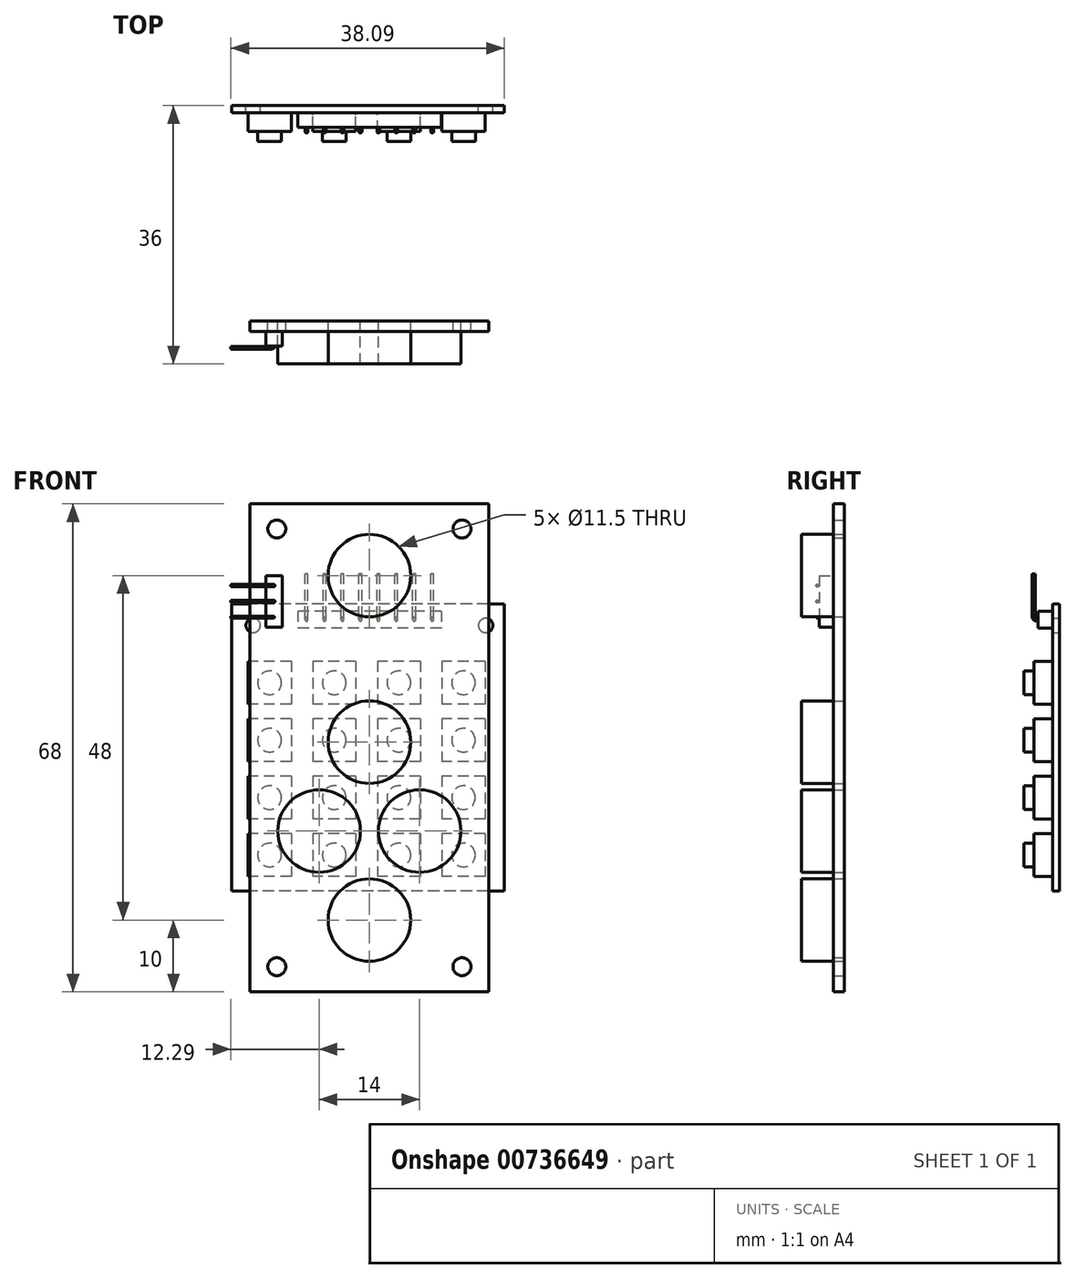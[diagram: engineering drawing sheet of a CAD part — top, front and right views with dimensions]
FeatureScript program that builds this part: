
annotation { "Feature Type Name" : "Feature", "Feature Type Description" : "" }
export const myFeature = defineFeature(function(context is Context, id is Id, definition is map)
    precondition{}
    {
        {
            var Q0;
            Q0=qCreatedBy(makeId("Front.planeOp"),FACE);
            var sketch = newSketch(context, id + "F0", { "sketchPlane" : qUnion([Q0])});
            skLineSegment(sketch, "E0.bottom", {"start": v(18.8, 20.06) * mm, "end": v(-19.2, 20.06) * mm});
            skLineSegment(sketch, "E0.top", {"start": v(18.8, -19.94) * mm, "end": v(-19.2, -19.94) * mm});
            skLineSegment(sketch, "E0.left", {"start": v(18.8, 20.06) * mm, "end": v(18.8, -19.94) * mm});
            skLineSegment(sketch, "E0.right", {"start": v(-19.2, 20.06) * mm, "end": v(-19.2, -19.94) * mm});
            skCircle(sketch, "E1", {"center": v(-16.2, 17.06) * mm, "radius": 1 * mm});
            skCircle(sketch, "E2.MirrorC", {"center": v(16.2, 17.06) * mm, "radius": 1 * mm});
            skLineSegment(sketch, "E3.bottom", {"start": v(-10.9, 12.06) * mm, "end": v(-16.9, 12.06) * mm});
            skLineSegment(sketch, "E3.top", {"start": v(-10.9, 6.06) * mm, "end": v(-16.9, 6.06) * mm});
            skLineSegment(sketch, "E3.left", {"start": v(-10.9, 12.06) * mm, "end": v(-10.9, 6.06) * mm});
            skLineSegment(sketch, "E3.right", {"start": v(-16.9, 12.06) * mm, "end": v(-16.9, 6.06) * mm});
            skPoint(sketch, "E3.middle", {"position": v(-13.9, 9.06) * mm});
            skCircle(sketch, "E4", {"center": v(-13.9, 9.06) * mm, "radius": 1.65 * mm});
            skLineSegment(sketch, "E5.0.1.0", {"start": v(-10.9, 4.06) * mm, "end": v(-10.9, -1.94) * mm});
            skLineSegment(sketch, "E5.0.1.1", {"start": v(-10.9, -1.94) * mm, "end": v(-16.9, -1.94) * mm});
            skLineSegment(sketch, "E5.0.1.2", {"start": v(-16.9, 4.06) * mm, "end": v(-16.9, -1.94) * mm});
            skLineSegment(sketch, "E5.0.1.3", {"start": v(-10.9, 4.06) * mm, "end": v(-16.9, 4.06) * mm});
            skCircle(sketch, "E5.0.1.4", {"center": v(-13.9, 1.06) * mm, "radius": 1.65 * mm});
            skLineSegment(sketch, "E5.0.2.0", {"start": v(-10.9, -3.94) * mm, "end": v(-10.9, -9.94) * mm});
            skLineSegment(sketch, "E5.0.2.1", {"start": v(-10.9, -9.94) * mm, "end": v(-16.9, -9.94) * mm});
            skLineSegment(sketch, "E5.0.2.2", {"start": v(-16.9, -3.94) * mm, "end": v(-16.9, -9.94) * mm});
            skLineSegment(sketch, "E5.0.2.3", {"start": v(-10.9, -3.94) * mm, "end": v(-16.9, -3.94) * mm});
            skCircle(sketch, "E5.0.2.4", {"center": v(-13.9, -6.94) * mm, "radius": 1.65 * mm});
            skLineSegment(sketch, "E5.0.3.0", {"start": v(-10.9, -11.94) * mm, "end": v(-10.9, -17.94) * mm});
            skLineSegment(sketch, "E5.0.3.1", {"start": v(-10.9, -17.94) * mm, "end": v(-16.9, -17.94) * mm});
            skLineSegment(sketch, "E5.0.3.2", {"start": v(-16.9, -11.94) * mm, "end": v(-16.9, -17.94) * mm});
            skLineSegment(sketch, "E5.0.3.3", {"start": v(-10.9, -11.94) * mm, "end": v(-16.9, -11.94) * mm});
            skCircle(sketch, "E5.0.3.4", {"center": v(-13.9, -14.94) * mm, "radius": 1.65 * mm});
            skLineSegment(sketch, "E5.1.0.0", {"start": v(-1.9, 12.06) * mm, "end": v(-1.9, 6.06) * mm});
            skLineSegment(sketch, "E5.1.0.1", {"start": v(-1.9, 6.06) * mm, "end": v(-7.9, 6.06) * mm});
            skLineSegment(sketch, "E5.1.0.2", {"start": v(-7.9, 12.06) * mm, "end": v(-7.9, 6.06) * mm});
            skLineSegment(sketch, "E5.1.0.3", {"start": v(-1.9, 12.06) * mm, "end": v(-7.9, 12.06) * mm});
            skCircle(sketch, "E5.1.0.4", {"center": v(-4.9, 9.06) * mm, "radius": 1.65 * mm});
            skLineSegment(sketch, "E5.1.1.0", {"start": v(-1.9, 4.06) * mm, "end": v(-1.9, -1.94) * mm});
            skLineSegment(sketch, "E5.1.1.1", {"start": v(-1.9, -1.94) * mm, "end": v(-7.9, -1.94) * mm});
            skLineSegment(sketch, "E5.1.1.2", {"start": v(-7.9, 4.06) * mm, "end": v(-7.9, -1.94) * mm});
            skLineSegment(sketch, "E5.1.1.3", {"start": v(-1.9, 4.06) * mm, "end": v(-7.9, 4.06) * mm});
            skCircle(sketch, "E5.1.1.4", {"center": v(-4.9, 1.06) * mm, "radius": 1.65 * mm});
            skLineSegment(sketch, "E5.1.2.0", {"start": v(-1.9, -3.94) * mm, "end": v(-1.9, -9.94) * mm});
            skLineSegment(sketch, "E5.1.2.1", {"start": v(-1.9, -9.94) * mm, "end": v(-7.9, -9.94) * mm});
            skLineSegment(sketch, "E5.1.2.2", {"start": v(-7.9, -3.94) * mm, "end": v(-7.9, -9.94) * mm});
            skLineSegment(sketch, "E5.1.2.3", {"start": v(-1.9, -3.94) * mm, "end": v(-7.9, -3.94) * mm});
            skCircle(sketch, "E5.1.2.4", {"center": v(-4.9, -6.94) * mm, "radius": 1.65 * mm});
            skLineSegment(sketch, "E5.1.3.0", {"start": v(-1.9, -11.94) * mm, "end": v(-1.9, -17.94) * mm});
            skLineSegment(sketch, "E5.1.3.1", {"start": v(-1.9, -17.94) * mm, "end": v(-7.9, -17.94) * mm});
            skLineSegment(sketch, "E5.1.3.2", {"start": v(-7.9, -11.94) * mm, "end": v(-7.9, -17.94) * mm});
            skLineSegment(sketch, "E5.1.3.3", {"start": v(-1.9, -11.94) * mm, "end": v(-7.9, -11.94) * mm});
            skCircle(sketch, "E5.1.3.4", {"center": v(-4.9, -14.94) * mm, "radius": 1.65 * mm});
            skLineSegment(sketch, "E5.2.0.0", {"start": v(7.1, 12.06) * mm, "end": v(7.1, 6.06) * mm});
            skLineSegment(sketch, "E5.2.0.1", {"start": v(7.1, 6.06) * mm, "end": v(1.1, 6.06) * mm});
            skLineSegment(sketch, "E5.2.0.2", {"start": v(1.1, 12.06) * mm, "end": v(1.1, 6.06) * mm});
            skLineSegment(sketch, "E5.2.0.3", {"start": v(7.1, 12.06) * mm, "end": v(1.1, 12.06) * mm});
            skCircle(sketch, "E5.2.0.4", {"center": v(4.1, 9.06) * mm, "radius": 1.65 * mm});
            skLineSegment(sketch, "E5.2.1.0", {"start": v(7.1, 4.06) * mm, "end": v(7.1, -1.94) * mm});
            skLineSegment(sketch, "E5.2.1.1", {"start": v(7.1, -1.94) * mm, "end": v(1.1, -1.94) * mm});
            skLineSegment(sketch, "E5.2.1.2", {"start": v(1.1, 4.06) * mm, "end": v(1.1, -1.94) * mm});
            skLineSegment(sketch, "E5.2.1.3", {"start": v(7.1, 4.06) * mm, "end": v(1.1, 4.06) * mm});
            skCircle(sketch, "E5.2.1.4", {"center": v(4.1, 1.06) * mm, "radius": 1.65 * mm});
            skLineSegment(sketch, "E5.2.2.0", {"start": v(7.1, -3.94) * mm, "end": v(7.1, -9.94) * mm});
            skLineSegment(sketch, "E5.2.2.1", {"start": v(7.1, -9.94) * mm, "end": v(1.1, -9.94) * mm});
            skLineSegment(sketch, "E5.2.2.2", {"start": v(1.1, -3.94) * mm, "end": v(1.1, -9.94) * mm});
            skLineSegment(sketch, "E5.2.2.3", {"start": v(7.1, -3.94) * mm, "end": v(1.1, -3.94) * mm});
            skCircle(sketch, "E5.2.2.4", {"center": v(4.1, -6.94) * mm, "radius": 1.65 * mm});
            skLineSegment(sketch, "E5.2.3.0", {"start": v(7.1, -11.94) * mm, "end": v(7.1, -17.94) * mm});
            skLineSegment(sketch, "E5.2.3.1", {"start": v(7.1, -17.94) * mm, "end": v(1.1, -17.94) * mm});
            skLineSegment(sketch, "E5.2.3.2", {"start": v(1.1, -11.94) * mm, "end": v(1.1, -17.94) * mm});
            skLineSegment(sketch, "E5.2.3.3", {"start": v(7.1, -11.94) * mm, "end": v(1.1, -11.94) * mm});
            skCircle(sketch, "E5.2.3.4", {"center": v(4.1, -14.94) * mm, "radius": 1.65 * mm});
            skLineSegment(sketch, "E5.3.0.0", {"start": v(16.1, 12.06) * mm, "end": v(16.1, 6.06) * mm});
            skLineSegment(sketch, "E5.3.0.1", {"start": v(16.1, 6.06) * mm, "end": v(10.1, 6.06) * mm});
            skLineSegment(sketch, "E5.3.0.2", {"start": v(10.1, 12.06) * mm, "end": v(10.1, 6.06) * mm});
            skLineSegment(sketch, "E5.3.0.3", {"start": v(16.1, 12.06) * mm, "end": v(10.1, 12.06) * mm});
            skCircle(sketch, "E5.3.0.4", {"center": v(13.1, 9.06) * mm, "radius": 1.65 * mm});
            skLineSegment(sketch, "E5.3.1.0", {"start": v(16.1, 4.06) * mm, "end": v(16.1, -1.94) * mm});
            skLineSegment(sketch, "E5.3.1.1", {"start": v(16.1, -1.94) * mm, "end": v(10.1, -1.94) * mm});
            skLineSegment(sketch, "E5.3.1.2", {"start": v(10.1, 4.06) * mm, "end": v(10.1, -1.94) * mm});
            skLineSegment(sketch, "E5.3.1.3", {"start": v(16.1, 4.06) * mm, "end": v(10.1, 4.06) * mm});
            skCircle(sketch, "E5.3.1.4", {"center": v(13.1, 1.06) * mm, "radius": 1.65 * mm});
            skLineSegment(sketch, "E5.3.2.0", {"start": v(16.1, -3.94) * mm, "end": v(16.1, -9.94) * mm});
            skLineSegment(sketch, "E5.3.2.1", {"start": v(16.1, -9.94) * mm, "end": v(10.1, -9.94) * mm});
            skLineSegment(sketch, "E5.3.2.2", {"start": v(10.1, -3.94) * mm, "end": v(10.1, -9.94) * mm});
            skLineSegment(sketch, "E5.3.2.3", {"start": v(16.1, -3.94) * mm, "end": v(10.1, -3.94) * mm});
            skCircle(sketch, "E5.3.2.4", {"center": v(13.1, -6.94) * mm, "radius": 1.65 * mm});
            skLineSegment(sketch, "E5.3.3.0", {"start": v(16.1, -11.94) * mm, "end": v(16.1, -17.94) * mm});
            skLineSegment(sketch, "E5.3.3.1", {"start": v(16.1, -17.94) * mm, "end": v(10.1, -17.94) * mm});
            skLineSegment(sketch, "E5.3.3.2", {"start": v(10.1, -11.94) * mm, "end": v(10.1, -17.94) * mm});
            skLineSegment(sketch, "E5.3.3.3", {"start": v(16.1, -11.94) * mm, "end": v(10.1, -11.94) * mm});
            skCircle(sketch, "E5.3.3.4", {"center": v(13.1, -14.94) * mm, "radius": 1.65 * mm});
            skLineSegment(sketch, "E5.direction1", {"start": v(-10.9, 6.06) * mm, "end": v(-1.9, 6.06) * mm, "construction": true});
            skLineSegment(sketch, "E5.direction2", {"start": v(-10.9, 6.06) * mm, "end": v(-10.9, -1.94) * mm, "construction": true});
            skLineSegment(sketch, "E6.bottom", {"start": v(10, 19.06) * mm, "end": v(-10, 19.06) * mm});
            skLineSegment(sketch, "E6.top", {"start": v(10, 16.66) * mm, "end": v(-10, 16.66) * mm});
            skLineSegment(sketch, "E6.left", {"start": v(10, 19.06) * mm, "end": v(10, 16.66) * mm});
            skLineSegment(sketch, "E6.right", {"start": v(-10, 19.06) * mm, "end": v(-10, 16.66) * mm});
            skPoint(sketch, "E6.middle", {"position": v(0, 17.86) * mm});
            skCircle(sketch, "E7", {"center": v(-8.75, 17.86) * mm, "radius": 0.2 * mm});
            skCircle(sketch, "E8.1.0.0", {"center": v(-6.25, 17.86) * mm, "radius": 0.2 * mm});
            skCircle(sketch, "E8.2.0.0", {"center": v(-3.75, 17.86) * mm, "radius": 0.2 * mm});
            skCircle(sketch, "E8.3.0.0", {"center": v(-1.25, 17.86) * mm, "radius": 0.2 * mm});
            skCircle(sketch, "E8.4.0.0", {"center": v(1.25, 17.86) * mm, "radius": 0.2 * mm});
            skCircle(sketch, "E8.5.0.0", {"center": v(3.75, 17.86) * mm, "radius": 0.2 * mm});
            skCircle(sketch, "E8.6.0.0", {"center": v(6.25, 17.86) * mm, "radius": 0.2 * mm});
            skCircle(sketch, "E8.7.0.0", {"center": v(8.75, 17.86) * mm, "radius": 0.2 * mm});
            skLineSegment(sketch, "E8.direction1", {"start": v(-8.75, 17.86) * mm, "end": v(-6.25, 17.86) * mm, "construction": true});
            skSolve(sketch);
        }
        {
            var Q0;
            Q0=makeQuery(id+"F0.imprint","IMPRINT",FACE,{"disambiguationData":[TD([[makeQuery(id+"F0.imprint","IMPRINT",EDGE,{"derivedFrom":sQuery(id+"F0.wireOp",EDGE,"E0.bottom")}),1.0]])]});
            extrude(context, id + "F1", {"entities" : qUnion([Q0]), "depth" : 1 * mm, "offsetDistance" : 25 * mm});
        }
        {
            var Q0;
            Q0=makeQuery(id+"F0.imprint","IMPRINT",FACE,{"disambiguationData":[TD([[makeQuery(id+"F0.imprint","IMPRINT",EDGE,{"derivedFrom":sQuery(id+"F0.wireOp",EDGE,"E3.bottom")}),1.0]])]});
            var Q1;
            Q1=makeQuery(id+"F0.imprint","IMPRINT",FACE,{"disambiguationData":[TD([[makeQuery(id+"F0.imprint","IMPRINT",EDGE,{"derivedFrom":sQuery(id+"F0.wireOp",EDGE,"E5.1.0.0")}),-1.0]])]});
            var Q2;
            Q2=makeQuery(id+"F0.imprint","IMPRINT",FACE,{"disambiguationData":[TD([[makeQuery(id+"F0.imprint","IMPRINT",EDGE,{"derivedFrom":sQuery(id+"F0.wireOp",EDGE,"E5.2.0.0")}),-1.0]])]});
            var Q3;
            Q3=makeQuery(id+"F0.imprint","IMPRINT",FACE,{"disambiguationData":[TD([[makeQuery(id+"F0.imprint","IMPRINT",EDGE,{"derivedFrom":sQuery(id+"F0.wireOp",EDGE,"E5.3.0.0")}),-1.0]])]});
            var Q4;
            Q4=makeQuery(id+"F0.imprint","IMPRINT",FACE,{"disambiguationData":[TD([[makeQuery(id+"F0.imprint","IMPRINT",EDGE,{"derivedFrom":sQuery(id+"F0.wireOp",EDGE,"E5.0.1.0")}),-1.0]])]});
            var Q5;
            Q5=makeQuery(id+"F0.imprint","IMPRINT",FACE,{"disambiguationData":[TD([[makeQuery(id+"F0.imprint","IMPRINT",EDGE,{"derivedFrom":sQuery(id+"F0.wireOp",EDGE,"E5.1.1.0")}),-1.0]])]});
            var Q6;
            Q6=makeQuery(id+"F0.imprint","IMPRINT",FACE,{"disambiguationData":[TD([[makeQuery(id+"F0.imprint","IMPRINT",EDGE,{"derivedFrom":sQuery(id+"F0.wireOp",EDGE,"E5.2.1.0")}),-1.0]])]});
            var Q7;
            Q7=makeQuery(id+"F0.imprint","IMPRINT",FACE,{"disambiguationData":[TD([[makeQuery(id+"F0.imprint","IMPRINT",EDGE,{"derivedFrom":sQuery(id+"F0.wireOp",EDGE,"E5.3.1.0")}),-1.0]])]});
            var Q8;
            Q8=makeQuery(id+"F0.imprint","IMPRINT",FACE,{"disambiguationData":[TD([[makeQuery(id+"F0.imprint","IMPRINT",EDGE,{"derivedFrom":sQuery(id+"F0.wireOp",EDGE,"E5.0.2.0")}),-1.0]])]});
            var Q9;
            Q9=makeQuery(id+"F0.imprint","IMPRINT",FACE,{"disambiguationData":[TD([[makeQuery(id+"F0.imprint","IMPRINT",EDGE,{"derivedFrom":sQuery(id+"F0.wireOp",EDGE,"E5.1.2.0")}),-1.0]])]});
            var Q10;
            Q10=makeQuery(id+"F0.imprint","IMPRINT",FACE,{"disambiguationData":[TD([[makeQuery(id+"F0.imprint","IMPRINT",EDGE,{"derivedFrom":sQuery(id+"F0.wireOp",EDGE,"E5.2.2.0")}),-1.0]])]});
            var Q11;
            Q11=makeQuery(id+"F0.imprint","IMPRINT",FACE,{"disambiguationData":[TD([[makeQuery(id+"F0.imprint","IMPRINT",EDGE,{"derivedFrom":sQuery(id+"F0.wireOp",EDGE,"E5.3.2.0")}),-1.0]])]});
            var Q12;
            Q12=makeQuery(id+"F0.imprint","IMPRINT",FACE,{"disambiguationData":[TD([[makeQuery(id+"F0.imprint","IMPRINT",EDGE,{"derivedFrom":sQuery(id+"F0.wireOp",EDGE,"E5.0.3.0")}),-1.0]])]});
            var Q13;
            Q13=makeQuery(id+"F0.imprint","IMPRINT",FACE,{"disambiguationData":[TD([[makeQuery(id+"F0.imprint","IMPRINT",EDGE,{"derivedFrom":sQuery(id+"F0.wireOp",EDGE,"E5.1.3.0")}),-1.0]])]});
            var Q14;
            Q14=makeQuery(id+"F0.imprint","IMPRINT",FACE,{"disambiguationData":[TD([[makeQuery(id+"F0.imprint","IMPRINT",EDGE,{"derivedFrom":sQuery(id+"F0.wireOp",EDGE,"E5.2.3.0")}),-1.0]])]});
            var Q15;
            Q15=makeQuery(id+"F0.imprint","IMPRINT",FACE,{"disambiguationData":[TD([[makeQuery(id+"F0.imprint","IMPRINT",EDGE,{"derivedFrom":sQuery(id+"F0.wireOp",EDGE,"E5.3.3.0")}),-1.0]])]});
            extrude(context, id + "F2", {"entities" : qUnion([Q0, Q1, Q2, Q3, Q4, Q5, Q6, Q7, Q8, Q9, Q10, Q11, Q12, Q13, Q14, Q15]), "operationType" : NewBodyOperationType.ADD, "depth" : 3.6 * mm, "offsetDistance" : 25 * mm});
        }
        {
            var Q0;
            Q0=makeQuery(id+"F0.imprint","IMPRINT",FACE,{"disambiguationData":[TD([[makeQuery(id+"F0.imprint","IMPRINT",EDGE,{"derivedFrom":sQuery(id+"F0.wireOp",EDGE,"E4")}),1.0]])]});
            var Q1;
            Q1=makeQuery(id+"F0.imprint","IMPRINT",FACE,{"disambiguationData":[TD([[makeQuery(id+"F0.imprint","IMPRINT",EDGE,{"derivedFrom":sQuery(id+"F0.wireOp",EDGE,"E5.1.0.4")}),1.0]])]});
            var Q2;
            Q2=makeQuery(id+"F0.imprint","IMPRINT",FACE,{"disambiguationData":[TD([[makeQuery(id+"F0.imprint","IMPRINT",EDGE,{"derivedFrom":sQuery(id+"F0.wireOp",EDGE,"E5.2.0.4")}),1.0]])]});
            var Q3;
            Q3=makeQuery(id+"F0.imprint","IMPRINT",FACE,{"disambiguationData":[TD([[makeQuery(id+"F0.imprint","IMPRINT",EDGE,{"derivedFrom":sQuery(id+"F0.wireOp",EDGE,"E5.3.0.4")}),1.0]])]});
            var Q4;
            Q4=makeQuery(id+"F0.imprint","IMPRINT",FACE,{"disambiguationData":[TD([[makeQuery(id+"F0.imprint","IMPRINT",EDGE,{"derivedFrom":sQuery(id+"F0.wireOp",EDGE,"E5.0.1.4")}),1.0]])]});
            var Q5;
            Q5=makeQuery(id+"F0.imprint","IMPRINT",FACE,{"disambiguationData":[TD([[makeQuery(id+"F0.imprint","IMPRINT",EDGE,{"derivedFrom":sQuery(id+"F0.wireOp",EDGE,"E5.1.1.4")}),1.0]])]});
            var Q6;
            Q6=makeQuery(id+"F0.imprint","IMPRINT",FACE,{"disambiguationData":[TD([[makeQuery(id+"F0.imprint","IMPRINT",EDGE,{"derivedFrom":sQuery(id+"F0.wireOp",EDGE,"E5.2.1.4")}),1.0]])]});
            var Q7;
            Q7=makeQuery(id+"F0.imprint","IMPRINT",FACE,{"disambiguationData":[TD([[makeQuery(id+"F0.imprint","IMPRINT",EDGE,{"derivedFrom":sQuery(id+"F0.wireOp",EDGE,"E5.3.1.4")}),1.0]])]});
            var Q8;
            Q8=makeQuery(id+"F0.imprint","IMPRINT",FACE,{"disambiguationData":[TD([[makeQuery(id+"F0.imprint","IMPRINT",EDGE,{"derivedFrom":sQuery(id+"F0.wireOp",EDGE,"E5.0.2.4")}),1.0]])]});
            var Q9;
            Q9=makeQuery(id+"F0.imprint","IMPRINT",FACE,{"disambiguationData":[TD([[makeQuery(id+"F0.imprint","IMPRINT",EDGE,{"derivedFrom":sQuery(id+"F0.wireOp",EDGE,"E5.1.2.4")}),1.0]])]});
            var Q10;
            Q10=makeQuery(id+"F0.imprint","IMPRINT",FACE,{"disambiguationData":[TD([[makeQuery(id+"F0.imprint","IMPRINT",EDGE,{"derivedFrom":sQuery(id+"F0.wireOp",EDGE,"E5.2.2.4")}),1.0]])]});
            var Q11;
            Q11=makeQuery(id+"F0.imprint","IMPRINT",FACE,{"disambiguationData":[TD([[makeQuery(id+"F0.imprint","IMPRINT",EDGE,{"derivedFrom":sQuery(id+"F0.wireOp",EDGE,"E5.3.2.4")}),1.0]])]});
            var Q12;
            Q12=makeQuery(id+"F0.imprint","IMPRINT",FACE,{"disambiguationData":[TD([[makeQuery(id+"F0.imprint","IMPRINT",EDGE,{"derivedFrom":sQuery(id+"F0.wireOp",EDGE,"E5.0.3.4")}),1.0]])]});
            var Q13;
            Q13=makeQuery(id+"F0.imprint","IMPRINT",FACE,{"disambiguationData":[TD([[makeQuery(id+"F0.imprint","IMPRINT",EDGE,{"derivedFrom":sQuery(id+"F0.wireOp",EDGE,"E5.1.3.4")}),1.0]])]});
            var Q14;
            Q14=makeQuery(id+"F0.imprint","IMPRINT",FACE,{"disambiguationData":[TD([[makeQuery(id+"F0.imprint","IMPRINT",EDGE,{"derivedFrom":sQuery(id+"F0.wireOp",EDGE,"E5.2.3.4")}),1.0]])]});
            var Q15;
            Q15=makeQuery(id+"F0.imprint","IMPRINT",FACE,{"disambiguationData":[TD([[makeQuery(id+"F0.imprint","IMPRINT",EDGE,{"derivedFrom":sQuery(id+"F0.wireOp",EDGE,"E5.3.3.4")}),1.0]])]});
            extrude(context, id + "F3", {"entities" : qUnion([Q0, Q1, Q2, Q3, Q4, Q5, Q6, Q7, Q8, Q9, Q10, Q11, Q12, Q13, Q14, Q15]), "operationType" : NewBodyOperationType.ADD, "depth" : 5 * mm, "offsetDistance" : 25 * mm});
        }
        {
            var Q0;
            Q0=makeQuery(id+"F0.imprint","IMPRINT",FACE,{"disambiguationData":[TD([[makeQuery(id+"F0.imprint","IMPRINT",EDGE,{"derivedFrom":sQuery(id+"F0.wireOp",EDGE,"E6.bottom")}),1.0]])]});
            extrude(context, id + "F4", {"entities" : qUnion([Q0]), "operationType" : NewBodyOperationType.ADD, "depth" : 3 * mm, "offsetDistance" : 25 * mm});
        }
        {
            var Q0;
            Q0=qCreatedBy(makeId("Right.planeOp"),FACE);
            var sketch = newSketch(context, id + "F5", { "sketchPlane" : qUnion([Q0])});
            skPoint(sketch, "E9", {"position": v(0, 17.86) * mm});
            skLineSegment(sketch, "E10", {"start": v(0, 17.86) * mm, "end": v(-2.8, 17.86) * mm});
            skLineSegment(sketch, "E11", {"start": v(-3.62, 18.22) * mm, "end": v(-3.62, 24.22) * mm});
            skFitSpline(sketch, "E12", {"points": [v(-2.8, 17.86) * mm, v(-3.4, 17.93) * mm, v(-3.62, 18.22) * mm], "startDerivative": vector(-1.7, 0.07) * mm, "endDerivative": vector(-0.18, 1.32) * mm});
            skSolve(sketch);
        }
        {
            var Q0;
            Q0=makeQuery(id+"F0.imprint","IMPRINT",FACE,{"disambiguationData":[TD([[makeQuery(id+"F0.imprint","IMPRINT",EDGE,{"derivedFrom":sQuery(id+"F0.wireOp",EDGE,"E7")}),1.0]])]});
            var Q1;
            Q1=makeQuery(id+"F0.imprint","IMPRINT",FACE,{"disambiguationData":[TD([[makeQuery(id+"F0.imprint","IMPRINT",EDGE,{"derivedFrom":sQuery(id+"F0.wireOp",EDGE,"E8.1.0.0")}),1.0]])]});
            var Q2;
            Q2=makeQuery(id+"F0.imprint","IMPRINT",FACE,{"disambiguationData":[TD([[makeQuery(id+"F0.imprint","IMPRINT",EDGE,{"derivedFrom":sQuery(id+"F0.wireOp",EDGE,"E8.2.0.0")}),1.0]])]});
            var Q3;
            Q3=makeQuery(id+"F0.imprint","IMPRINT",FACE,{"disambiguationData":[TD([[makeQuery(id+"F0.imprint","IMPRINT",EDGE,{"derivedFrom":sQuery(id+"F0.wireOp",EDGE,"E8.3.0.0")}),1.0]])]});
            var Q4;
            Q4=makeQuery(id+"F0.imprint","IMPRINT",FACE,{"disambiguationData":[TD([[makeQuery(id+"F0.imprint","IMPRINT",EDGE,{"derivedFrom":sQuery(id+"F0.wireOp",EDGE,"E8.4.0.0")}),1.0]])]});
            var Q5;
            Q5=makeQuery(id+"F0.imprint","IMPRINT",FACE,{"disambiguationData":[TD([[makeQuery(id+"F0.imprint","IMPRINT",EDGE,{"derivedFrom":sQuery(id+"F0.wireOp",EDGE,"E8.5.0.0")}),1.0]])]});
            var Q6;
            Q6=makeQuery(id+"F0.imprint","IMPRINT",FACE,{"disambiguationData":[TD([[makeQuery(id+"F0.imprint","IMPRINT",EDGE,{"derivedFrom":sQuery(id+"F0.wireOp",EDGE,"E8.6.0.0")}),1.0]])]});
            var Q7;
            Q7=makeQuery(id+"F0.imprint","IMPRINT",FACE,{"disambiguationData":[TD([[makeQuery(id+"F0.imprint","IMPRINT",EDGE,{"derivedFrom":sQuery(id+"F0.wireOp",EDGE,"E8.7.0.0")}),1.0]])]});
            var Q8;
            Q8 = qConstructionFilter(qBodyType(qCreatedBy(id + "F5" ,EDGE), BodyType.WIRE), ConstructionObject.NO);
            sweep(context, id + "F6", {"operationType" : NewBodyOperationType.ADD, "profiles" : qUnion([Q0, Q1, Q2, Q3, Q4, Q5, Q6, Q7]), "path" : qUnion([Q8])});
        }
        {
            var Q0;
            Q0=qCreatedBy(makeId("Front.planeOp"),FACE);
            cPlane(context, id + "F7", {"entities" : qUnion([Q0]), "cplaneType" : CPlaneType.OFFSET, "offset" : 30 * mm, "width" : 150 * mm, "height" : 150 * mm});
        }
        {
            var Q0;
            Q0=qCreatedBy(id+"F7.planeOp",FACE);
            var sketch = newSketch(context, id + "F8", { "sketchPlane" : qUnion([Q0])});
            skLineSegment(sketch, "E13.bottom", {"start": v(16.65, 34) * mm, "end": v(-16.65, 34) * mm});
            skLineSegment(sketch, "E13.top", {"start": v(16.65, -34) * mm, "end": v(-16.65, -34) * mm});
            skLineSegment(sketch, "E13.left", {"start": v(16.65, 34) * mm, "end": v(16.65, -34) * mm});
            skLineSegment(sketch, "E13.right", {"start": v(-16.65, 34) * mm, "end": v(-16.65, -34) * mm});
            skPoint(sketch, "E13.middle", {"position": v(0, 0) * mm});
            skLineSegment(sketch, "E14.bottom", {"start": v(12.9, 30.5) * mm, "end": v(-12.9, 30.5) * mm, "construction": true});
            skLineSegment(sketch, "E14.top", {"start": v(12.9, -30.5) * mm, "end": v(-12.9, -30.5) * mm, "construction": true});
            skLineSegment(sketch, "E14.left", {"start": v(12.9, 30.5) * mm, "end": v(12.9, -30.5) * mm, "construction": true});
            skLineSegment(sketch, "E14.right", {"start": v(-12.9, 30.5) * mm, "end": v(-12.9, -30.5) * mm, "construction": true});
            skCircle(sketch, "E15", {"center": v(-12.9, 30.5) * mm, "radius": 1.25 * mm});
            skCircle(sketch, "E16", {"center": v(12.9, 30.5) * mm, "radius": 1.25 * mm});
            skCircle(sketch, "E17", {"center": v(12.9, -30.5) * mm, "radius": 1.25 * mm});
            skCircle(sketch, "E18", {"center": v(-12.9, -30.5) * mm, "radius": 1.25 * mm});
            skPoint(sketch, "E19", {"position": v(0, 24) * mm});
            skPoint(sketch, "E20", {"position": v(0, -24) * mm});
            skPoint(sketch, "E21", {"position": v(0, 0.8) * mm});
            skPoint(sketch, "E22", {"position": v(-7, -11.6) * mm});
            skPoint(sketch, "E23.MirrorP", {"position": v(7, -11.6) * mm});
            skCircle(sketch, "E24", {"center": v(0, 24) * mm, "radius": 5.75 * mm});
            skCircle(sketch, "E25", {"center": v(0, 0.8) * mm, "radius": 5.75 * mm});
            skCircle(sketch, "E26", {"center": v(7, -11.6) * mm, "radius": 5.75 * mm});
            skCircle(sketch, "E27", {"center": v(0, -24) * mm, "radius": 5.75 * mm});
            skCircle(sketch, "E28", {"center": v(-7, -11.6) * mm, "radius": 5.75 * mm});
            skLineSegment(sketch, "E29.bottom", {"start": v(-12.15, 24) * mm, "end": v(-14.45, 24) * mm});
            skLineSegment(sketch, "E29.top", {"start": v(-12.15, 16.8) * mm, "end": v(-14.45, 16.8) * mm});
            skLineSegment(sketch, "E29.left", {"start": v(-12.15, 24) * mm, "end": v(-12.15, 16.8) * mm});
            skLineSegment(sketch, "E29.right", {"start": v(-14.45, 24) * mm, "end": v(-14.45, 16.8) * mm});
            skPoint(sketch, "E29.middle", {"position": v(-13.3, 20.4) * mm});
            skCircle(sketch, "E30", {"center": v(-13.3, 20.4) * mm, "radius": 0.15 * mm});
            skCircle(sketch, "E31", {"center": v(-13.3, 22.6) * mm, "radius": 0.15 * mm});
            skCircle(sketch, "E32", {"center": v(-13.37, 18.2) * mm, "radius": 0.15 * mm});
            skSolve(sketch);
        }
        {
            var Q0;
            Q0=makeQuery(id+"F8.imprint","IMPRINT",FACE,{"disambiguationData":[TD([[makeQuery(id+"F8.imprint","IMPRINT",EDGE,{"derivedFrom":sQuery(id+"F8.wireOp",EDGE,"E13.bottom")}),1.0]])]});
            extrude(context, id + "F9", {"entities" : qUnion([Q0]), "depth" : 1.5 * mm, "offsetDistance" : 25 * mm});
        }
        {
            var Q0;
            Q0=makeQuery(id+"F8.imprint","IMPRINT",FACE,{"disambiguationData":[TD([[makeQuery(id+"F8.imprint","IMPRINT",EDGE,{"derivedFrom":sQuery(id+"F8.wireOp",EDGE,"E24")}),1.0]])]});
            var Q1;
            Q1=makeQuery(id+"F8.imprint","IMPRINT",FACE,{"disambiguationData":[TD([[makeQuery(id+"F8.imprint","IMPRINT",EDGE,{"derivedFrom":sQuery(id+"F8.wireOp",EDGE,"E25")}),1.0]])]});
            var Q2;
            Q2=makeQuery(id+"F8.imprint","IMPRINT",FACE,{"disambiguationData":[TD([[makeQuery(id+"F8.imprint","IMPRINT",EDGE,{"derivedFrom":sQuery(id+"F8.wireOp",EDGE,"E26")}),1.0]])]});
            var Q3;
            Q3=makeQuery(id+"F8.imprint","IMPRINT",FACE,{"disambiguationData":[TD([[makeQuery(id+"F8.imprint","IMPRINT",EDGE,{"derivedFrom":sQuery(id+"F8.wireOp",EDGE,"E28")}),1.0]])]});
            var Q4;
            Q4=makeQuery(id+"F8.imprint","IMPRINT",FACE,{"disambiguationData":[TD([[makeQuery(id+"F8.imprint","IMPRINT",EDGE,{"derivedFrom":sQuery(id+"F8.wireOp",EDGE,"E27")}),1.0]])]});
            extrude(context, id + "F10", {"entities" : qUnion([Q0, Q1, Q2, Q3, Q4]), "depth" : 6 * mm, "offsetDistance" : 25 * mm});
        }
        {
            var Q0;
            Q0=makeQuery(id+"F8.imprint","IMPRINT",FACE,{"disambiguationData":[TD([[makeQuery(id+"F8.imprint","IMPRINT",EDGE,{"derivedFrom":sQuery(id+"F8.wireOp",EDGE,"E29.bottom")}),1.0]])]});
            extrude(context, id + "F11", {"entities" : qUnion([Q0]), "operationType" : NewBodyOperationType.ADD, "depth" : 3.5 * mm, "offsetDistance" : 25 * mm});
        }
        {
            var Q0;
            Q0=qCreatedBy(makeId("Top.planeOp"),FACE);
            var sketch = newSketch(context, id + "F12", { "sketchPlane" : qUnion([Q0])});
            skLineSegment(sketch, "E33", {"start": v(-13.3, -33.5) * mm, "end": v(-13.3, -30) * mm});
            skLineSegment(sketch, "E34.MirrorCS", {"start": v(-19.29, -33.8) * mm, "end": v(-13.79, -33.8) * mm});
            skFitSpline(sketch, "E35.MirrorCS", {"points": [v(-13.79, -33.8) * mm, v(-13.43, -33.73) * mm, v(-13.3, -33.5) * mm], "startDerivative": vector(1, 0.04) * mm, "endDerivative": vector(0.1, 0.77) * mm});
            skSolve(sketch);
        }
        {
            var Q0;
            Q0=makeQuery(id+"F8.imprint","IMPRINT",FACE,{"disambiguationData":[TD([[makeQuery(id+"F8.imprint","IMPRINT",EDGE,{"derivedFrom":sQuery(id+"F8.wireOp",EDGE,"E31")}),1.0]])]});
            var Q1;
            Q1=makeQuery(id+"F8.imprint","IMPRINT",FACE,{"disambiguationData":[TD([[makeQuery(id+"F8.imprint","IMPRINT",EDGE,{"derivedFrom":sQuery(id+"F8.wireOp",EDGE,"E30")}),1.0]])]});
            var Q2;
            Q2=makeQuery(id+"F8.imprint","IMPRINT",FACE,{"disambiguationData":[TD([[makeQuery(id+"F8.imprint","IMPRINT",EDGE,{"derivedFrom":sQuery(id+"F8.wireOp",EDGE,"E32")}),1.0]])]});
            var Q3;
            Q3=sQuery(id+"F12.wireOp",EDGE,"E33");
            var Q4;
            Q4=sQuery(id+"F12.wireOp",EDGE,"E35.MirrorCS");
            var Q5;
            Q5=sQuery(id+"F12.wireOp",EDGE,"E34.MirrorCS");
            sweep(context, id + "F13", {"operationType" : NewBodyOperationType.ADD, "profiles" : qUnion([Q0, Q1, Q2]), "path" : qUnion([Q3, Q4, Q5])});
        }
    });
